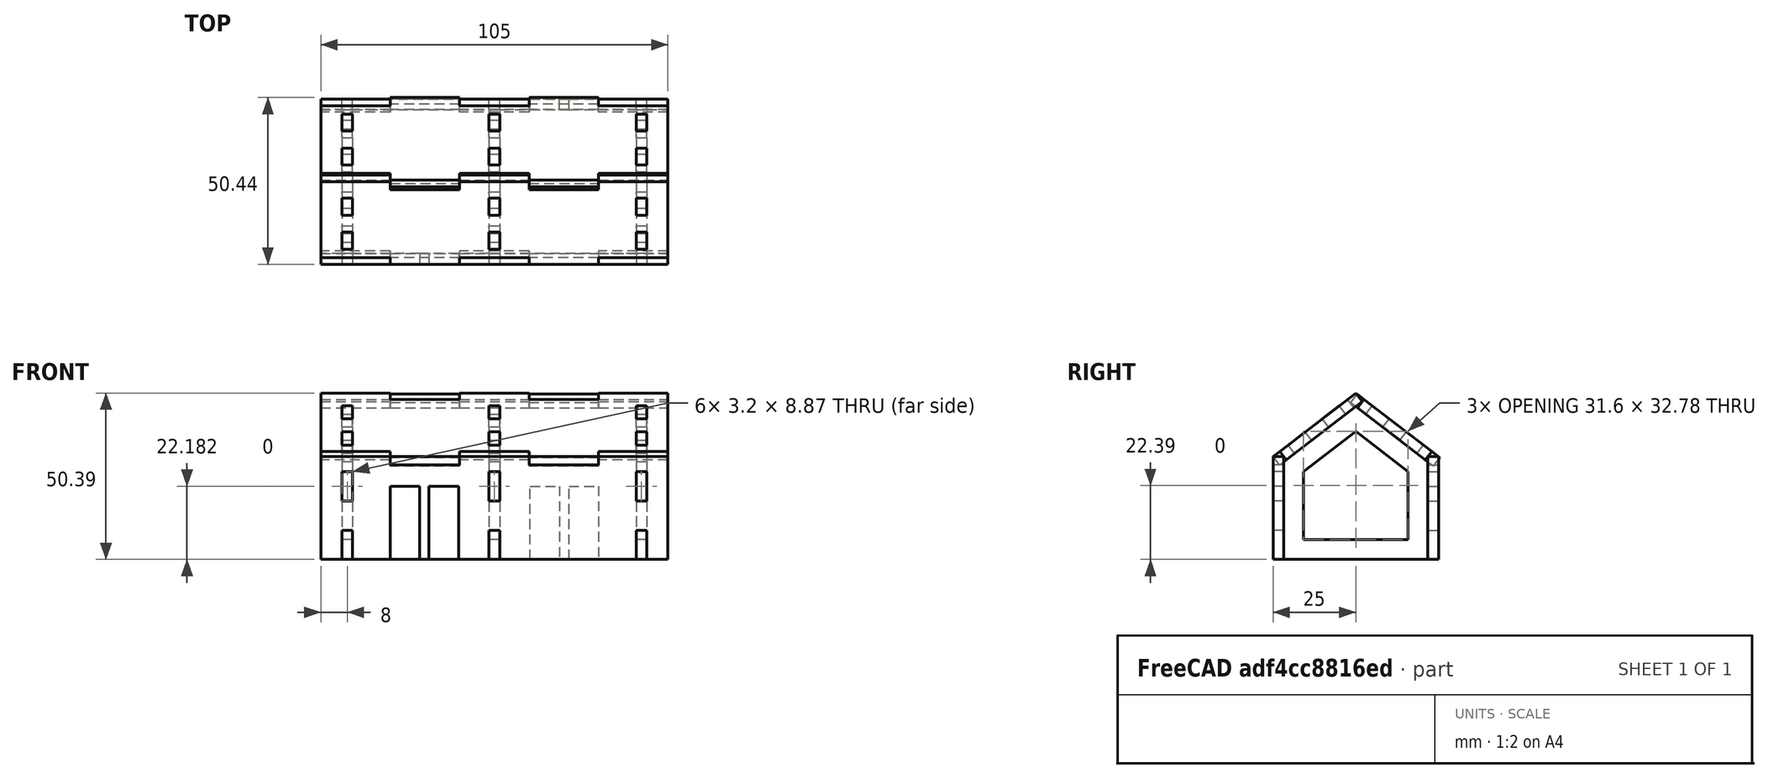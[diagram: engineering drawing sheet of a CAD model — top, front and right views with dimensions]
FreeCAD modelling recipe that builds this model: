
FCSTD DOCUMENT  (FreeCAD 0.17R10885 (Git))
Label: maquete
License: All rights reserved
LicenseURL: http://en.wikipedia.org/wiki/All_rights_reserved
objects: Part::Feature×20, Part::Cut×18, Part::FeaturePython×7, App::FeaturePython×3, Part::Part2DObjectPython×2, App::DocumentObjectGroup×1
note: 47 computed .brp shape members not serialized (recipe doc carries the construction recipe); baked Part::Feature solids carry a one-line shape summary decoded from their .brp

FEATURE [Part::Feature] Polyline003
  shape: bbox 3.2 x 8.873 x 2e-07 mm, 1 faces, 0 solids (baked)
FEATURE [Part::Feature] Polyline004
  shape: bbox 3.2 x 8.873 x 2e-07 mm, 1 faces, 0 solids (baked)
FEATURE [Part::Feature] Polyline005
  shape: bbox 3.2 x 8.873 x 2e-07 mm, 1 faces, 0 solids (baked)
FEATURE [Part::Feature] Polyline006
  shape: bbox 105 x 31.54 x 2e-07 mm, 1 faces, 0 solids (baked)
FEATURE [Part::Feature] Polyline007
  shape: bbox 3.2 x 6.504 x 2e-07 mm, 1 faces, 0 solids (baked)
FEATURE [Part::Feature] Polyline008
  shape: bbox 105 x 31.54 x 2e-07 mm, 1 faces, 0 solids (baked)
FEATURE [Part::Feature] Polyline009 .. Polyline019  x11 (patterned run collapsed; names and placements below)
  shape: bbox 3.2 x 6.504 x 2e-07 mm, 1 faces, 0 solids (baked)
FEATURE [Part::Feature] Polyline020
  shape: bbox 31.6 x 32.78 x 2e-07 mm, 1 faces, 0 solids (baked)
FEATURE [Part::Feature] Polyline021
  shape: bbox 50 x 46.55 x 2e-07 mm, 1 faces, 0 solids (baked)
FEATURE [Part::Cut] Cut
  Base = -> Polyline021
  Tool = -> Polyline020
FEATURE [Part::Feature] Polyline002
  shape: bbox 105 x 31.16 x 2e-07 mm, 1 faces, 0 solids (baked)
FEATURE [App::DocumentObjectGroup] NEW
  Group = -> [Polyline002,Polyline003,Polyline004,Polyline005,Polyline006,Polyline007,Polyline008,Polyline009,Polyline010,Polyline011,Polyline012,Polyline013,Polyline014,Polyline015,Polyline016,Polyline017,Polyline018,Polyline019,Polyline020,Polyline021]
FEATURE [Part::Cut] Cut001
  Base = -> Polyline002
  Tool = -> Polyline003
FEATURE [Part::Cut] Cut002
  Base = -> Cut001
  Tool = -> Polyline004
FEATURE [Part::Cut] Cut003
  Base = -> Cut002
  Tool = -> Polyline005
FEATURE [Part::Cut] Cut004
  Base = -> Polyline006
  Tool = -> Polyline018
FEATURE [Part::Cut] Cut005
  Base = -> Cut004
  Tool = -> Polyline019
FEATURE [Part::Cut] Cut006
  Base = -> Cut005
  Tool = -> Polyline016
FEATURE [Part::Cut] Cut007
  Base = -> Cut006
  Tool = -> Polyline017
FEATURE [Part::Cut] Cut008
  Base = -> Cut007
  Tool = -> Polyline015
FEATURE [Part::Cut] Cut009
  Base = -> Cut008
  Tool = -> Polyline014
FEATURE [Part::Cut] Cut010
  Base = -> Polyline008
  Tool = -> Polyline012
FEATURE [Part::Cut] Cut011
  Base = -> Cut010
  Tool = -> Polyline013
FEATURE [Part::Cut] Cut012
  Base = -> Cut011
  Tool = -> Polyline010
FEATURE [Part::Cut] Cut013
  Base = -> Cut012
  Tool = -> Polyline011
FEATURE [Part::Cut] Cut014
  Base = -> Cut013
  Tool = -> Polyline007
FEATURE [Part::Cut] Cut015
  Base = -> Cut014
  Tool = -> Polyline009
FEATURE [Part::FeaturePython] Panel  # WARN: FeaturePython — macro-defined, semantics opaque (R4)
  Area = 1008.27
  Base = -> Cut
  FaceMaker = 0
  HorizontalArea = 0
  Length = 0
  MoveWithHost = false
  Normal = (0,0,1)
  PerimeterLength = 0
  Placement = pos=(3.2,-79.8693,-171.96) rot=(0.57735,0.57735,-0.57735;4.18879rad)
  Role = 0
  Sheets = 1
  Thickness = 3.2
  VerticalArea = 0
  WaveDirection = 0
  WaveHeight = 0
  WaveLength = 0
  WaveType = 0
  Width = 0
FEATURE [Part::FeaturePython] Panel002  # WARN: FeaturePython — macro-defined, semantics opaque (R4)
  Area = 2832.26
  Base = -> Cut015
  FaceMaker = 0
  HorizontalArea = 0
  Length = 0
  MoveWithHost = false
  Normal = (0,0,1)
  PerimeterLength = 0
  Placement = pos=(33.1246,11.0693,-96.7816) rot=(-1,0,0;0.655696rad)
  Role = 0
  Sheets = 1
  Thickness = 3.2
  VerticalArea = 0
  WaveDirection = 0
  WaveHeight = 0
  WaveLength = 0
  WaveType = 0
  Width = 0
FEATURE [Part::FeaturePython] Panel003  # WARN: FeaturePython — macro-defined, semantics opaque (R4)
  Area = 2897.21
  Base = -> Cut009
  FaceMaker = 0
  HorizontalArea = 0
  Length = 0
  MoveWithHost = false
  Normal = (0,0,1)
  PerimeterLength = 0
  Placement = pos=(33.1246,16.1156,193.361) rot=(1,0,0;0.655696rad)
  Role = 0
  Sheets = 1
  Thickness = 3.2
  VerticalArea = 0
  WaveDirection = 0
  WaveHeight = 0
  WaveLength = 0
  WaveType = 0
  Width = 0
FEATURE [Part::FeaturePython] Panel004  # WARN: FeaturePython — macro-defined, semantics opaque (R4)
  Area = 1008.27
  CloneOf = -> Panel
  FaceMaker = 0
  HorizontalArea = 0
  Length = 0
  MoveWithHost = false
  Normal = (0,0,0)
  PerimeterLength = 0
  Placement = pos=(47.7,-79.8693,-171.96) rot=(0.57735,0.57735,-0.57735;4.18879rad)
  Role = 0
  Sheets = 1
  Thickness = 3.2
  VerticalArea = 0
  WaveDirection = 0
  WaveHeight = 0
  WaveLength = 0
  WaveType = 0
  Width = 0
FEATURE [Part::FeaturePython] Panel005  # WARN: FeaturePython — macro-defined, semantics opaque (R4)
  Area = 1008.27
  CloneOf = -> Panel
  FaceMaker = 0
  HorizontalArea = 0
  Length = 0
  MoveWithHost = false
  Normal = (0,0,0)
  PerimeterLength = 0
  Placement = pos=(92.2,-79.8693,-171.96) rot=(0.57735,0.57735,-0.57735;4.18879rad)
  Role = 0
  Sheets = 1
  Thickness = 3.2
  VerticalArea = 0
  WaveDirection = 0
  WaveHeight = 0
  WaveLength = 0
  WaveType = 0
  Width = 0
FEATURE [Part::Part2DObjectPython] Rectangle  # Draft 2D object (typed FeaturePython)
  ChamferSize = 0
  Columns = 1
  FilletRadius = 0
  Height = 22.2
  Length = 8.9
  MakeFace = true
  Placement = pos=(-6.77464,-303.352,0) rot=(0,0,1;0rad)
  Rows = 1
FEATURE [Part::Part2DObjectPython] Rectangle001  # Draft 2D object (typed FeaturePython)
  ChamferSize = 0
  Columns = 1
  FilletRadius = 0
  Height = 22.2
  Length = 8.9
  MakeFace = true
  Placement = pos=(-18.5246,-303.352,0) rot=(0,0,1;0rad)
  Rows = 1
FEATURE [Part::Cut] Cut016
  Base = -> Cut003
  Tool = -> Rectangle
FEATURE [Part::Cut] Cut017
  Base = -> Cut016
  Tool = -> Rectangle001
FEATURE [Part::FeaturePython] Panel001  # WARN: FeaturePython — macro-defined, semantics opaque (R4)
  Area = 2599.24
  Base = -> Cut017
  FaceMaker = 0
  HorizontalArea = 0
  Length = 0
  MoveWithHost = false
  Normal = (0,0,1)
  PerimeterLength = 0
  Placement = pos=(33.1246,-196.8,303.352) rot=(1,0,0;1.5708rad)
  Role = 0
  Sheets = 1
  Thickness = 3.2
  VerticalArea = 0
  WaveDirection = 0
  WaveHeight = 0
  WaveLength = 0
  WaveType = 0
  Width = 0
FEATURE [Part::FeaturePython] Panel006  # WARN: FeaturePython — macro-defined, semantics opaque (R4)
  Area = 2599.24
  CloneOf = -> Panel001
  FaceMaker = 0
  HorizontalArea = 0
  Length = 0
  MoveWithHost = false
  Normal = (0,0,0)
  PerimeterLength = 0
  Placement = pos=(59.0754,-153.2,303.352) rot=(0,0.707107,0.707107;3.14159rad)
  Role = 0
  Sheets = 1
  Thickness = 3.2
  VerticalArea = 0
  WaveDirection = 0
  WaveHeight = 0
  WaveLength = 0
  WaveType = 0
  Width = 0
FEATURE [App::FeaturePython] Dimension  # Draft dimension (typed FeaturePython)
  Diameter = false
  Dimline = (-17.9631,-160.8,0)
  Direction = (0,0,0)
  Distance = 50
  End = (-6.4,-150,0)
  Normal = (0,0,1)
  Start = (-6.4,-200,0)
FEATURE [App::FeaturePython] Dimension001  # Draft dimension (typed FeaturePython)
  Diameter = false
  Dimline = (90.59,-133.633,0)
  Direction = (0,0,0)
  Distance = 105
  End = (98.6,-150,0)
  Normal = (0,0,1)
  Start = (-6.4,-150,0)
FEATURE [App::FeaturePython] Dimension002  # Draft dimension (typed FeaturePython)
  Diameter = false
  Dimline = (-17.9631,-150,0)
  Direction = (0,0,0)
  Distance = 50.3859
  End = (-6.4,-150,50.3859)
  Normal = (0,1,0)
  Start = (-6.4,-150,0)
